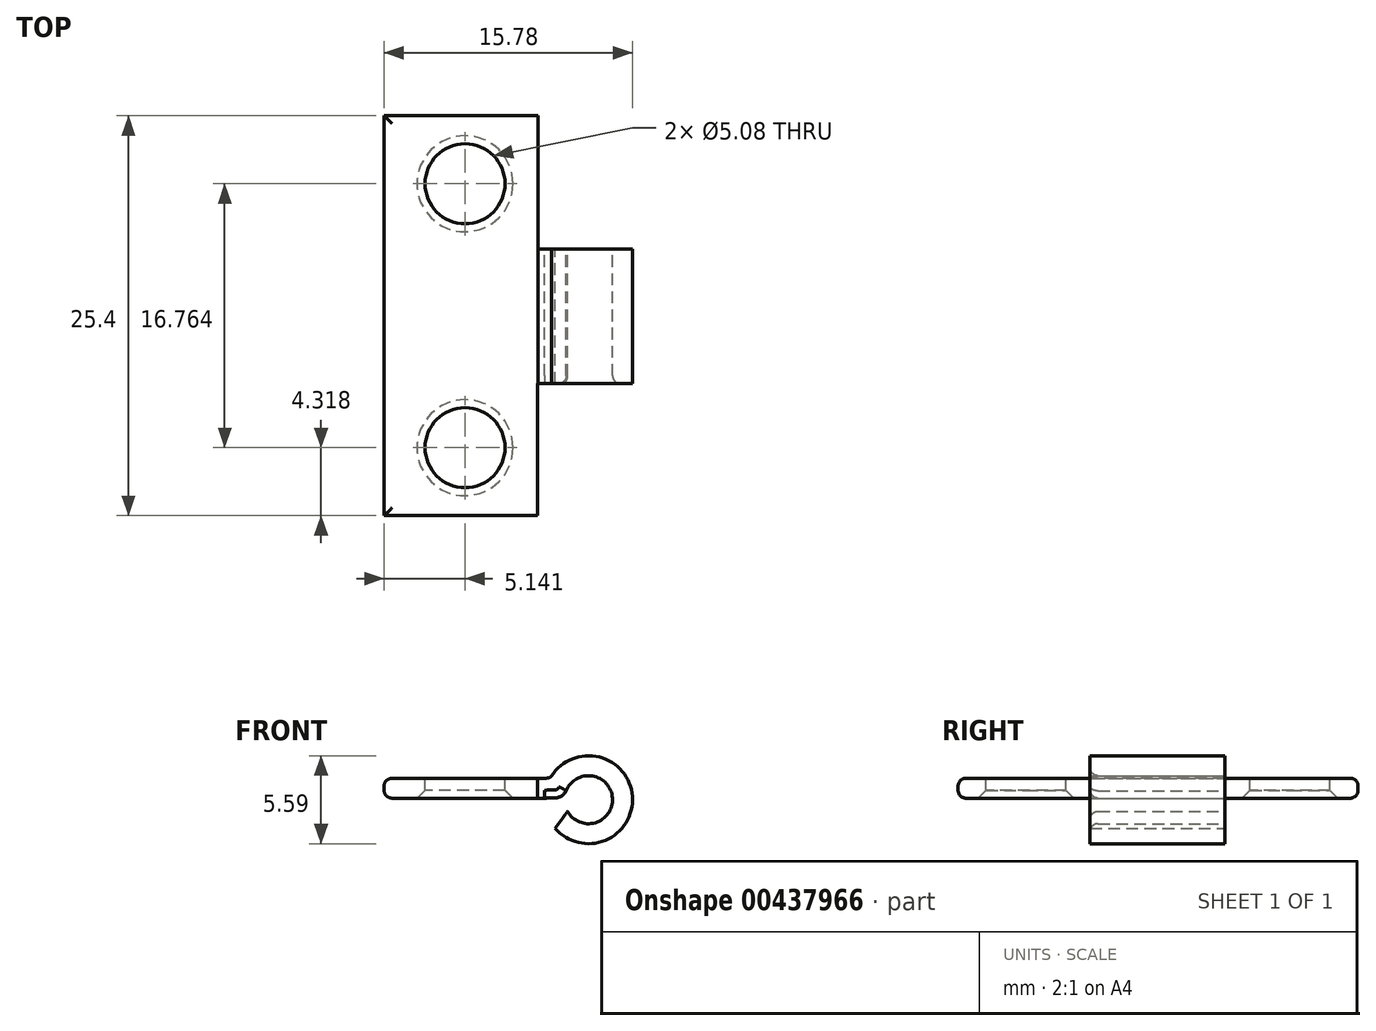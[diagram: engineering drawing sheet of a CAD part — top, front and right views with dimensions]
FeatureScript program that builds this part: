
annotation { "Feature Type Name" : "Feature", "Feature Type Description" : "" }
export const myFeature = defineFeature(function(context is Context, id is Id, definition is map)
    precondition{}
    {
        {
            var Q0;
            Q0=qCreatedBy(makeId("Front.planeOp"),FACE);
            var sketch = newSketch(context, id + "F0", { "sketchPlane" : qUnion([Q0])});
            skLineSegment(sketch, "E0.bottom", {"start": v(-28.78, 12.85) * mm, "end": v(-19, 12.85) * mm});
            skLineSegment(sketch, "E0.top", {"start": v(-28.78, 11.58) * mm, "end": v(-18.59, 11.58) * mm});
            skLineSegment(sketch, "E0.left", {"start": v(-28.78, 12.85) * mm, "end": v(-28.78, 11.58) * mm});
            skArc(sketch, "E1", {"start": v(-17.91, 9.66) * mm, "mid": v(-13, 11.69) * mm, "end": v(-18.15, 12.99) * mm});
            skPoint(sketch, "E1.centerSnap0", {"position": v(-18.61, 11.49) * mm});
            skArc(sketch, "E2", {"start": v(-17.13, 10.75) * mm, "mid": v(-14.27, 11.59) * mm, "end": v(-17.21, 12.05) * mm});
            skFitSpline(sketch, "E3", {"points": [v(-17.21, 12.05) * mm, v(-17.65, 11.65) * mm, v(-18.59, 11.58) * mm], "startDerivative": vector(-1.12, -1.46) * mm, "endDerivative": vector(-2.02, -0.1) * mm});
            skLineSegment(sketch, "E4", {"start": v(-17.13, 10.75) * mm, "end": v(-17.91, 9.66) * mm});
            skFitSpline(sketch, "E5", {"points": [v(-19, 12.85) * mm, v(-18.59, 12.85) * mm, v(-18.15, 12.99) * mm], "startDerivative": vector(0.67, 0) * mm, "endDerivative": vector(0.6, 0.75) * mm});
            skSolve(sketch);
        }
        {
            var Q0;
            Q0=qSketchRegion(id+"F0",true);
            extrude(context, id + "F1", {"entities" : qUnion([Q0]), "depth" : 25.4 * mm});
        }
        {
            var Q0;
            Q0=makeQuery(id+"F1.opExtrude","SWEPT_FACE",FACE,{"disambiguationData":[OSD([sQuery(id+"F0.wireOp",EDGE,"E0.bottom")])]});
            var sketch = newSketch(context, id + "F2", { "sketchPlane" : qUnion([Q0])});
            skLineSegment(sketch, "E6.bottom", {"start": v(-19.02, -17.02) * mm, "end": v(-10.92, -17.02) * mm});
            skLineSegment(sketch, "E6.top", {"start": v(-19.02, -25.4) * mm, "end": v(-10.92, -25.4) * mm});
            skLineSegment(sketch, "E6.left", {"start": v(-19.02, -17.02) * mm, "end": v(-19.02, -25.4) * mm});
            skLineSegment(sketch, "E6.right", {"start": v(-10.92, -17.02) * mm, "end": v(-10.92, -25.4) * mm});
            skLineSegment(sketch, "E7.bottom", {"start": v(-19, 0) * mm, "end": v(-9.4, 0) * mm});
            skLineSegment(sketch, "E7.top", {"start": v(-19, -8.46) * mm, "end": v(-9.4, -8.46) * mm});
            skLineSegment(sketch, "E7.left", {"start": v(-19, 0) * mm, "end": v(-19, -8.46) * mm});
            skLineSegment(sketch, "E7.right", {"start": v(-9.4, 0) * mm, "end": v(-9.4, -8.46) * mm});
            skSolve(sketch);
        }
        {
            var Q0;
            Q0=qSketchRegion(id+"F2",true);
            extrude(context, id + "F3", {"entities" : qUnion([Q0]), "operationType" : NewBodyOperationType.REMOVE, "oppositeDirection" : true, "depth" : 25.4 * mm, "symmetric" : true});
        }
        {
            var Q0;
            Q0=makeQuery(id+"F1.opExtrude","CAP_EDGE",EDGE,{"disambiguationData":[OSD([sQuery(id+"F0.wireOp",EDGE,"E0.bottom")])],"isStart":false});
            var Q1;
            Q1=makeQuery(id+"F1.opExtrude","SWEPT_EDGE",EDGE,{"disambiguationData":[OSD([sQuery(id+"F0.wireOp",EDGE,"E0.bottom"),sQuery(id+"F0.wireOp",EDGE,"E0.left")])]});
            var Q2;
            Q2=makeQuery(id+"F1.opExtrude","CAP_EDGE",EDGE,{"disambiguationData":[OSD([sQuery(id+"F0.wireOp",EDGE,"E0.bottom")])],"isStart":true});
            var Q3;
            Q3=makeQuery(id+"F1.opExtrude","CAP_EDGE",EDGE,{"disambiguationData":[OSD([sQuery(id+"F0.wireOp",EDGE,"E0.top")])],"isStart":false});
            var Q4;
            Q4=makeQuery(id+"F1.opExtrude","SWEPT_EDGE",EDGE,{"disambiguationData":[OSD([sQuery(id+"F0.wireOp",EDGE,"E0.top"),sQuery(id+"F0.wireOp",EDGE,"E0.left")])]});
            var Q5;
            Q5=makeQuery(id+"F1.opExtrude","CAP_EDGE",EDGE,{"disambiguationData":[OSD([sQuery(id+"F0.wireOp",EDGE,"E0.top")])],"isStart":true});
            var Q6;
            Q6=makeQuery(id+"F3.boolean.opBoolean","INTERSECT",EDGE,{"derivedFrom":[makeQuery(id+"F1.opExtrude","SWEPT_FACE",FACE,{"disambiguationData":[OSD([sQuery(id+"F0.wireOp",EDGE,"E0.top")])]}),makeQuery(id+"F3.opExtrude","SWEPT_FACE",FACE,{"disambiguationData":[OSD([sQuery(id+"F2.wireOp",EDGE,"E6.top")])]})]});
            var Q7;
            Q7=makeQuery(id+"F3.boolean.opBoolean","INTERSECT",EDGE,{"derivedFrom":[makeQuery(id+"F1.opExtrude","SWEPT_FACE",FACE,{"disambiguationData":[OSD([sQuery(id+"F0.wireOp",EDGE,"E3")])]}),makeQuery(id+"F3.opExtrude","SWEPT_FACE",FACE,{"disambiguationData":[OSD([sQuery(id+"F2.wireOp",EDGE,"E6.bottom")])]})]});
            var Q8;
            Q8=makeQuery(id+"F3.boolean.opBoolean","INTERSECT",EDGE,{"derivedFrom":[makeQuery(id+"F1.opExtrude","SWEPT_FACE",FACE,{"disambiguationData":[OSD([sQuery(id+"F0.wireOp",EDGE,"E0.top")])]}),makeQuery(id+"F3.opExtrude","SWEPT_FACE",FACE,{"disambiguationData":[OSD([sQuery(id+"F2.wireOp",EDGE,"E6.bottom")])]})]});
            var Q9;
            Q9=makeQuery(id+"F3.boolean.opBoolean","INTERSECT",EDGE,{"derivedFrom":[makeQuery(id+"F1.opExtrude","SWEPT_FACE",FACE,{"disambiguationData":[OSD([sQuery(id+"F0.wireOp",EDGE,"E2")])]}),makeQuery(id+"F3.opExtrude","SWEPT_FACE",FACE,{"disambiguationData":[OSD([sQuery(id+"F2.wireOp",EDGE,"E6.bottom")])]})]});
            var Q10;
            Q10=makeQuery(id+"F3.boolean.opBoolean","INTERSECT",EDGE,{"derivedFrom":[makeQuery(id+"F1.opExtrude","SWEPT_FACE",FACE,{"disambiguationData":[OSD([sQuery(id+"F0.wireOp",EDGE,"E2")])]}),makeQuery(id+"F3.opExtrude","SWEPT_FACE",FACE,{"disambiguationData":[OSD([sQuery(id+"F2.wireOp",EDGE,"E6.top")])]})]});
            fillet(context, id + "F4", {"entities" : qUnion([Q0, Q1, Q2, Q3, Q4, Q5, Q6, Q7, Q8, Q9, Q10]), "radius" : 0.5 * mm, "tangentPropagation" : true, "allowEdgeOverflow" : false});
        }
        {
            var Q0;
            Q0=makeQuery(id+"F1.opExtrude","SWEPT_FACE",FACE,{"disambiguationData":[OSD([sQuery(id+"F0.wireOp",EDGE,"E0.bottom")])]});
            var sketch = newSketch(context, id + "F5", { "sketchPlane" : qUnion([Q0])});
            skCircle(sketch, "E8", {"center": v(-23.64, -4.32) * mm, "radius": 2.54 * mm});
            skPoint(sketch, "E8.centerSnap0", {"position": v(-23.64, -0.5) * mm});
            skCircle(sketch, "E9", {"center": v(-23.64, -21.08) * mm, "radius": 2.54 * mm});
            skSolve(sketch);
        }
        {
            var Q0;
            Q0=qSketchRegion(id+"F5",true);
            extrude(context, id + "F6", {"entities" : qUnion([Q0]), "operationType" : NewBodyOperationType.REMOVE, "oppositeDirection" : true, "depth" : 25.4 * mm});
        }
        {
            var Q0;
            Q0=makeQuery(id+"F6.boolean.opBoolean","COPY",EDGE,{"derivedFrom":makeQuery(id+"F6.opExtrude","CAP_EDGE",EDGE,{"disambiguationData":[OSD([sQuery(id+"F5.wireOp",EDGE,"E8")])],"isStart":true})});
            var Q1;
            Q1=makeQuery(id+"F6.boolean.opBoolean","INTERSECT",EDGE,{"derivedFrom":[makeQuery(id+"F1.opExtrude","SWEPT_FACE",FACE,{"disambiguationData":[OSD([sQuery(id+"F0.wireOp",EDGE,"E0.top")])]}),makeQuery(id+"F6.opExtrude","SWEPT_FACE",FACE,{"disambiguationData":[OSD([sQuery(id+"F5.wireOp",EDGE,"E8")])]})]});
            var Q2;
            Q2=makeQuery(id+"F6.boolean.opBoolean","COPY",EDGE,{"derivedFrom":makeQuery(id+"F6.opExtrude","CAP_EDGE",EDGE,{"disambiguationData":[OSD([sQuery(id+"F5.wireOp",EDGE,"E9")])],"isStart":true})});
            var Q3;
            Q3=makeQuery(id+"F6.boolean.opBoolean","INTERSECT",EDGE,{"derivedFrom":[makeQuery(id+"F1.opExtrude","SWEPT_FACE",FACE,{"disambiguationData":[OSD([sQuery(id+"F0.wireOp",EDGE,"E0.top")])]}),makeQuery(id+"F6.opExtrude","SWEPT_FACE",FACE,{"disambiguationData":[OSD([sQuery(id+"F5.wireOp",EDGE,"E9")])]})]});
            chamfer(context, id + "F7", {"entities" : qUnion([Q0, Q1, Q2, Q3]), "width" : 0.5 * mm, "tangentPropagation" : true});
        }
    });
